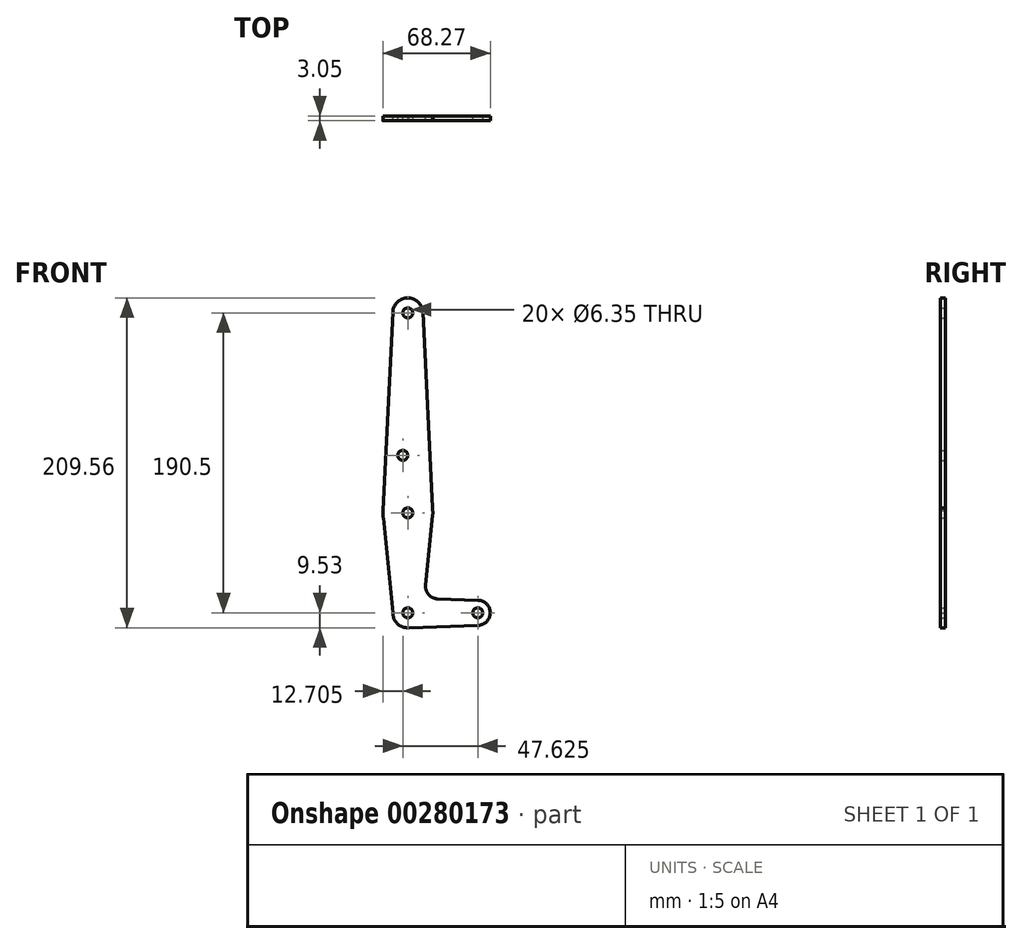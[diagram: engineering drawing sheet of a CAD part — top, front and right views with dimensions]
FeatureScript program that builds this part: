
annotation { "Feature Type Name" : "Feature", "Feature Type Description" : "" }
export const myFeature = defineFeature(function(context is Context, id is Id, definition is map)
    precondition{}
    {
        {
            var Q0;
            Q0=qCreatedBy(makeId("Front.planeOp"),FACE);
            var sketch = newSketch(context, id + "F0", { "sketchPlane" : qUnion([Q0])});
            skCircle(sketch, "E0", {"center": v(0, 0) * mm, "radius": 9.53 * mm});
            skLineSegment(sketch, "E1", {"start": v(0, 0) * mm, "end": v(0, 190.5) * mm, "construction": true});
            skCircle(sketch, "E2", {"center": v(0, 190.5) * mm, "radius": 9.53 * mm});
            skCircle(sketch, "E3", {"center": v(0, 63.5) * mm, "radius": 15.88 * mm});
            skLineSegment(sketch, "E4", {"start": v(0, 0) * mm, "end": v(44.45, 0) * mm, "construction": true});
            skCircle(sketch, "E5", {"center": v(44.45, 0) * mm, "radius": 7.94 * mm});
            skLineSegment(sketch, "E6", {"start": v(0, 63.5) * mm, "end": v(-24.99, 63.5) * mm});
            skLineSegment(sketch, "E7", {"start": v(0, 0) * mm, "end": v(-24.5, 0) * mm});
            skLineSegment(sketch, "E8", {"start": v(-15.88, 63.5) * mm, "end": v(-9.51, 190.97) * mm});
            skLineSegment(sketch, "E9", {"start": v(-15.88, 63.5) * mm, "end": v(-9.52, 0) * mm});
            skPoint(sketch, "E9.endSnap0", {"position": v(-12.25, 0) * mm});
            skLineSegment(sketch, "E10", {"start": v(18.93, 8.85) * mm, "end": v(44.73, 7.93) * mm});
            skLineSegment(sketch, "E11", {"start": v(0, -9.53) * mm, "end": v(44.73, -7.93) * mm});
            skLineSegment(sketch, "E12", {"start": v(11.3, 17.6) * mm, "end": v(15.8, 61.9) * mm});
            skLineSegment(sketch, "E13", {"start": v(15.8, 61.9) * mm, "end": v(9.51, 190.96) * mm});
            skCircle(sketch, "E14", {"center": v(0, 190.5) * mm, "radius": 3.18 * mm});
            skCircle(sketch, "E15", {"center": v(0, 0) * mm, "radius": 3.18 * mm});
            skCircle(sketch, "E16", {"center": v(0, 63.5) * mm, "radius": 3.18 * mm});
            skCircle(sketch, "E17", {"center": v(44.45, 0) * mm, "radius": 3.18 * mm});
            skCircle(sketch, "E18", {"center": v(-3.18, 100.03) * mm, "radius": 3.18 * mm});
            skLineSegment(sketch, "E19", {"start": v(-3.18, 100.03) * mm, "end": v(45.52, 100.03) * mm});
            skLineSegment(sketch, "E20", {"start": v(0, 63.5) * mm, "end": v(45.52, 63.5) * mm});
            skArc(sketch, "E21.filletArc", {"start": v(11.3, 17.6) * mm, "mid": v(13.22, 11.57) * mm, "end": v(18.93, 8.85) * mm});
            skSolve(sketch);
        }
        {
            var Q0;
            Q0 = qSketchRegion(id + "F0", true);
            extrude(context, id + "F1", {"entities" : qUnion([Q0]), "depth" : 3.05 * mm});
        }
    });
